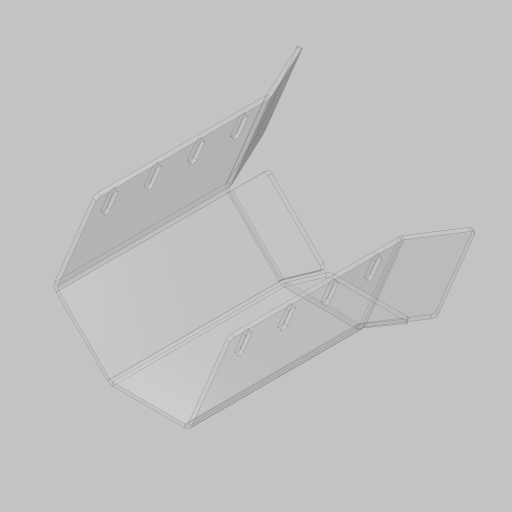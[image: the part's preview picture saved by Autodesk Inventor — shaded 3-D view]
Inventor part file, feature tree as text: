
AUTODESK INVENTOR PART (.ipt)
format: ipt  version: 2023.5 (Build 275446000, 446)  size: 288,256 bytes
history: native  units: in
note: dims shown in document units (in); Inventor stores cm internally (conversion verified against a paired STEP export)
features: sheet_metal_op x11, sketch x6, other x4, extrude x1, fillet x1
ambient origin geometry x8: Origin, YZ Plane, XZ Plane, XY Plane, X Axis, Y Axis, Z Axis, Center Point
bodies: Solid1 (feature_tree)
feature tree (23):
  sheet_metal_op  "Face1"
  sheet_metal_op  "Fold1"
  sheet_metal_op  "Flange1"
  sheet_metal_op  "Flange2"
  sheet_metal_op  "Flange3"
  extrude  "Extrusion1"  Depth=0.125in
  fillet  "Fillet1"  Radius=0.125in
  sketch  "Sketch1"  dims[d0=5.5in d1=6.0in d2=0.125in]
  other  "Plate1"
  sketch  "Sketch2"  dims[d3=0.125in]
  sketch  "Sketch3"  dims[d4=0.0625in]
  other  "Plate2"
  sheet_metal_op  "Bend1"
  sheet_metal_op  "Corner1"
  sketch  "Sketch4"  dims[d5=0.25in]
  other  "Plate3"
  sheet_metal_op  "Bend2"
  sheet_metal_op  "Corner2"
  sketch  "Sketch5"  dims[d6=0.125in]
  other  "Plate4"
  sheet_metal_op  "Bend3"
  sheet_metal_op  "Corner3"
  sketch  "Sketch7"  dims[d7=45.0deg d8=0.125in d9=0.125in d10=0.0625in d11=0.25in d12=0.125in d13=3.75in d14=67.5deg d15=0.125in d16=0.5in d17=0.125in d18=0.125in d19=0.125in d20=0.0625in d21=0.25in d22=0.125in d23=3.75in d24=67.5deg d25=0.125in d26=0.5in d27=0.125in d28=0.125in d29=0.125in d30=0.0625in d31=0.25in d32=0.125in d33=2.0in d34=22.5deg d35=0.125in d36=0.5in d37=0.125in d38=0.125in d50=0.201in d53=0.75in d54=1.5748in d56=1.5in d57=0.3937in d59=1.0in d61=0.0in d62=0.0in d63=0.75in d71=0.125in d72=2.5in]
